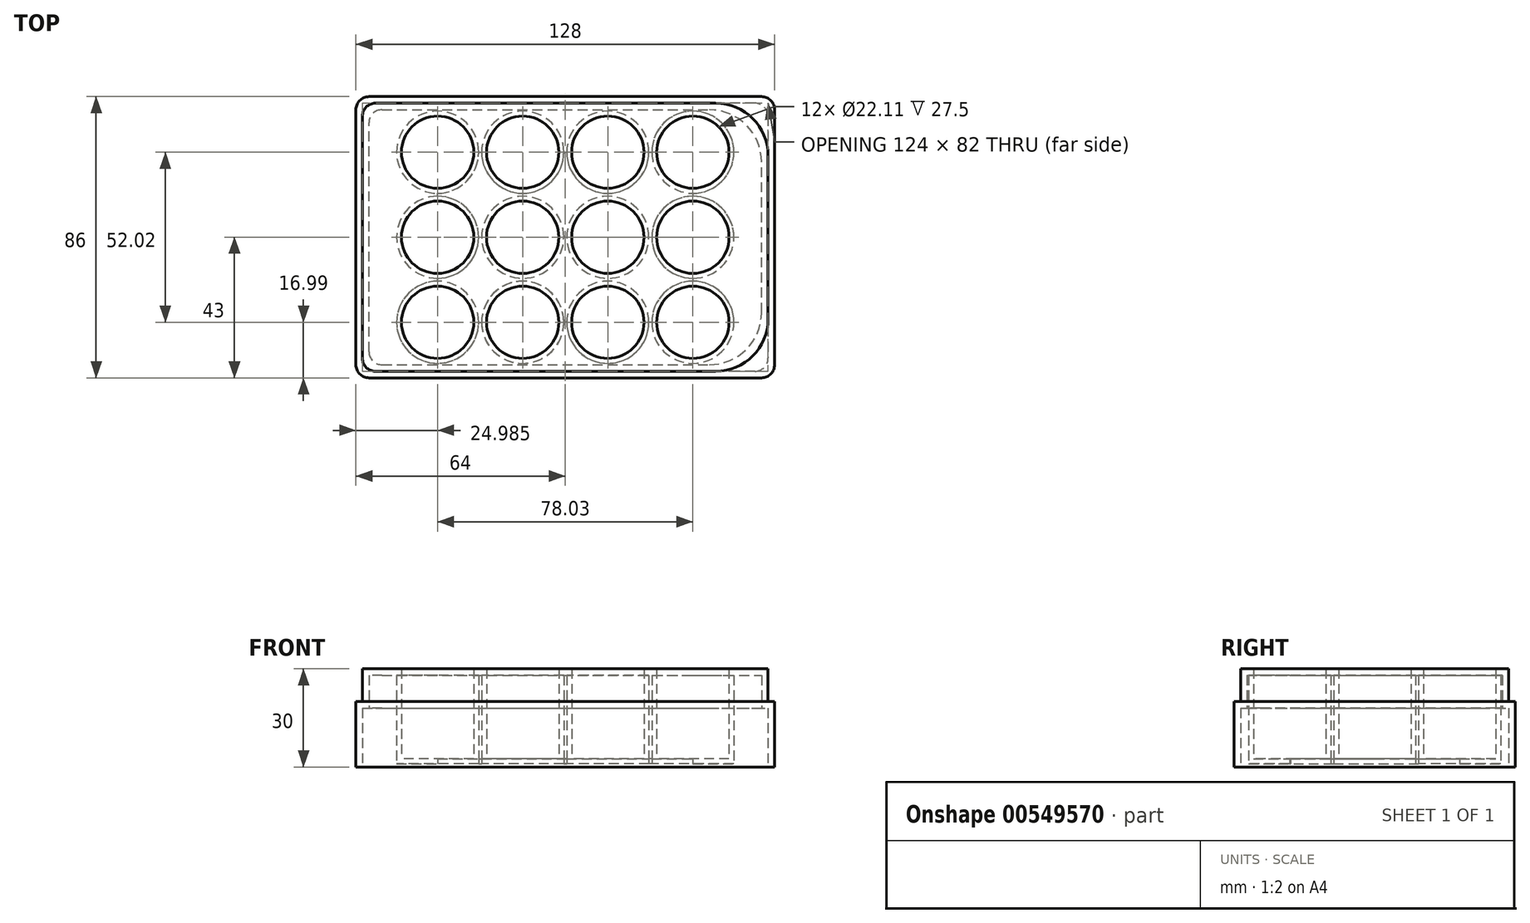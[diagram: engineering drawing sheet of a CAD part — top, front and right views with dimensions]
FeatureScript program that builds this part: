
annotation { "Feature Type Name" : "Feature", "Feature Type Description" : "" }
export const myFeature = defineFeature(function(context is Context, id is Id, definition is map)
    precondition{}
    {
        {
            var Q0;
            Q0=qCreatedBy(makeId("Top.planeOp"),FACE);
            var sketch = newSketch(context, id + "F0", { "sketchPlane" : qUnion([Q0])});
            skLineSegment(sketch, "E0.bottom", {"start": v(60, 43) * mm, "end": v(-60, 43) * mm});
            skLineSegment(sketch, "E0.top", {"start": v(64, -43) * mm, "end": v(-64, -43) * mm, "construction": true});
            skLineSegment(sketch, "E0.left", {"start": v(64, 39) * mm, "end": v(64, -39) * mm});
            skLineSegment(sketch, "E0.right", {"start": v(-64, 43) * mm, "end": v(-64, -39) * mm, "construction": true});
            skPoint(sketch, "E0.middle", {"position": v(0, 0) * mm});
            skLineSegment(sketch, "E1", {"start": v(-64, 26.01) * mm, "end": v(64, 26.01) * mm, "construction": true});
            skLineSegment(sketch, "E2", {"start": v(-64, 0) * mm, "end": v(64, 0) * mm, "construction": true});
            skLineSegment(sketch, "E3", {"start": v(-64, -26.01) * mm, "end": v(64, -26) * mm, "construction": true});
            skLineSegment(sketch, "E4", {"start": v(-39.02, -43) * mm, "end": v(-39.02, 43) * mm, "construction": true});
            skLineSegment(sketch, "E5", {"start": v(-13, -43) * mm, "end": v(-13, 43) * mm, "construction": true});
            skLineSegment(sketch, "E6", {"start": v(13, -43) * mm, "end": v(13, 43) * mm, "construction": true});
            skLineSegment(sketch, "E7", {"start": v(39.02, -43) * mm, "end": v(39.02, 43) * mm, "construction": true});
            skCircle(sketch, "E8", {"center": v(-39.02, 26.01) * mm, "radius": 11.05 * mm});
            skCircle(sketch, "E9", {"center": v(-13, 26.01) * mm, "radius": 11.05 * mm});
            skCircle(sketch, "E10", {"center": v(13, 26.01) * mm, "radius": 11.05 * mm});
            skCircle(sketch, "E11", {"center": v(39.02, 26.01) * mm, "radius": 11.05 * mm});
            skCircle(sketch, "E12", {"center": v(-13, 0) * mm, "radius": 11.05 * mm});
            skCircle(sketch, "E13", {"center": v(13, 0) * mm, "radius": 11.05 * mm});
            skCircle(sketch, "E14", {"center": v(39.02, 0) * mm, "radius": 11.05 * mm});
            skCircle(sketch, "E15", {"center": v(-13, -26) * mm, "radius": 11.05 * mm});
            skCircle(sketch, "E16", {"center": v(13, -26) * mm, "radius": 11.05 * mm});
            skCircle(sketch, "E17", {"center": v(39.02, -26) * mm, "radius": 11.05 * mm});
            skCircle(sketch, "E18", {"center": v(-39.02, 0) * mm, "radius": 11.05 * mm});
            skCircle(sketch, "E19", {"center": v(-39.02, -26) * mm, "radius": 11.05 * mm});
            skLineSegment(sketch, "E20", {"start": v(-64, 39) * mm, "end": v(-64, 26.01) * mm, "construction": true});
            skLineSegment(sketch, "E21", {"start": v(-64, 26.01) * mm, "end": v(-64, 0) * mm, "construction": true});
            skLineSegment(sketch, "E22", {"start": v(-64, 0) * mm, "end": v(-64, -26.01) * mm, "construction": true});
            skLineSegment(sketch, "E23", {"start": v(-60, -43) * mm, "end": v(-39.02, -43) * mm, "construction": true});
            skLineSegment(sketch, "E24", {"start": v(-39.02, -43) * mm, "end": v(-13, -43) * mm, "construction": true});
            skLineSegment(sketch, "E25", {"start": v(-13, -43) * mm, "end": v(13, -43) * mm, "construction": true});
            skLineSegment(sketch, "E26", {"start": v(13, -43) * mm, "end": v(39.02, -43) * mm, "construction": true});
            skLineSegment(sketch, "E27", {"start": v(39.02, -43) * mm, "end": v(60, -43) * mm, "construction": true});
            skPoint(sketch, "E28.visualSharp", {"position": v(-64, 43) * mm});
            skArc(sketch, "E28.filletArc", {"start": v(-60, 43) * mm, "mid": v(-62.83, 41.83) * mm, "end": v(-64, 39) * mm});
            skPoint(sketch, "E29.visualSharp", {"position": v(-64, -43) * mm});
            skArc(sketch, "E29.filletArc", {"start": v(-64, -39) * mm, "mid": v(-62.83, -41.83) * mm, "end": v(-60, -43) * mm});
            skPoint(sketch, "E30.visualSharp", {"position": v(64, -43) * mm});
            skArc(sketch, "E30.filletArc", {"start": v(60, -43) * mm, "mid": v(62.83, -41.83) * mm, "end": v(64, -39) * mm});
            skPoint(sketch, "E31.visualSharp", {"position": v(64, 43) * mm});
            skArc(sketch, "E31.filletArc", {"start": v(64, 39) * mm, "mid": v(62.83, 41.83) * mm, "end": v(60, 43) * mm});
            skLineSegment(sketch, "E32", {"start": v(-64, -39) * mm, "end": v(-64, -26.01) * mm, "construction": true});
            skLineSegment(sketch, "E33", {"start": v(-64, 39) * mm, "end": v(-64, -39) * mm});
            skLineSegment(sketch, "E34", {"start": v(-60, -43) * mm, "end": v(60, -43) * mm});
            skLineSegment(sketch, "E35.bottom", {"start": v(46, 41) * mm, "end": v(-58, 41) * mm});
            skLineSegment(sketch, "E35.top", {"start": v(46, -41) * mm, "end": v(-58, -41) * mm});
            skLineSegment(sketch, "E35.left", {"start": v(62, 25) * mm, "end": v(62, -25) * mm});
            skLineSegment(sketch, "E35.right", {"start": v(-62, 37) * mm, "end": v(-62, -37) * mm});
            skPoint(sketch, "E36.visualSharp", {"position": v(-62, 41) * mm});
            skArc(sketch, "E36.filletArc", {"start": v(-58, 41) * mm, "mid": v(-60.83, 39.83) * mm, "end": v(-62, 37) * mm});
            skPoint(sketch, "E37.visualSharp", {"position": v(-62, -41) * mm});
            skArc(sketch, "E37.filletArc", {"start": v(-62, -37) * mm, "mid": v(-60.83, -39.83) * mm, "end": v(-58, -41) * mm});
            skPoint(sketch, "E38.visualSharp", {"position": v(62, -41) * mm});
            skArc(sketch, "E38.filletArc", {"start": v(46, -41) * mm, "mid": v(57.31, -36.31) * mm, "end": v(62, -25) * mm});
            skPoint(sketch, "E39.visualSharp", {"position": v(62, 41) * mm});
            skArc(sketch, "E39.filletArc", {"start": v(62, 25) * mm, "mid": v(57.31, 36.31) * mm, "end": v(46, 41) * mm});
            skLineSegment(sketch, "E40", {"start": v(-58, 41) * mm, "end": v(58, 41) * mm});
            skLineSegment(sketch, "E41", {"start": v(62, 37) * mm, "end": v(62, -37) * mm});
            skLineSegment(sketch, "E42", {"start": v(58, -41) * mm, "end": v(-58, -41) * mm});
            skArc(sketch, "E43.filletArc", {"start": v(62, 37) * mm, "mid": v(60.83, 39.83) * mm, "end": v(58, 41) * mm});
            skArc(sketch, "E44.filletArc", {"start": v(58, -41) * mm, "mid": v(60.83, -39.83) * mm, "end": v(62, -37) * mm});
            skLineSegment(sketch, "E45.bottom", {"start": v(-56, -39) * mm, "end": v(44, -39) * mm});
            skLineSegment(sketch, "E45.top", {"start": v(-56, 39) * mm, "end": v(44, 39) * mm});
            skLineSegment(sketch, "E45.left", {"start": v(-60, -35) * mm, "end": v(-60, 35) * mm});
            skLineSegment(sketch, "E45.right", {"start": v(60, -23) * mm, "end": v(60, 23) * mm});
            skArc(sketch, "E46.filletArc", {"start": v(-60, -35) * mm, "mid": v(-58.83, -37.83) * mm, "end": v(-56, -39) * mm});
            skArc(sketch, "E47.filletArc", {"start": v(-56, 39) * mm, "mid": v(-58.83, 37.83) * mm, "end": v(-60, 35) * mm});
            skArc(sketch, "E48.filletArc", {"start": v(60, 23) * mm, "mid": v(55.31, 34.31) * mm, "end": v(44, 39) * mm});
            skArc(sketch, "E49.filletArc", {"start": v(44, -39) * mm, "mid": v(55.31, -34.31) * mm, "end": v(60, -23) * mm});
            skCircle(sketch, "E50", {"center": v(-39.02, -26) * mm, "radius": 12.55 * mm});
            skCircle(sketch, "E51", {"center": v(-13, 0) * mm, "radius": 12.55 * mm});
            skCircle(sketch, "E52", {"center": v(-13, 26) * mm, "radius": 12.55 * mm});
            skCircle(sketch, "E53", {"center": v(13, -26.01) * mm, "radius": 12.55 * mm});
            skCircle(sketch, "E54", {"center": v(13, 0) * mm, "radius": 12.55 * mm});
            skCircle(sketch, "E55", {"center": v(13, 26) * mm, "radius": 12.55 * mm});
            skCircle(sketch, "E56", {"center": v(39.02, -26.01) * mm, "radius": 12.55 * mm});
            skCircle(sketch, "E57", {"center": v(39.02, 26) * mm, "radius": 12.55 * mm});
            skCircle(sketch, "E58", {"center": v(39.02, 0) * mm, "radius": 12.55 * mm});
            skCircle(sketch, "E59", {"center": v(-13, -26.01) * mm, "radius": 12.55 * mm});
            skCircle(sketch, "E60", {"center": v(-39.02, 26) * mm, "radius": 12.55 * mm});
            skCircle(sketch, "E61", {"center": v(-39.02, 0) * mm, "radius": 12.55 * mm});
            skLineSegment(sketch, "E62", {"start": v(-39.02, -13.46) * mm, "end": v(-39.02, -12.56) * mm});
            skLineSegment(sketch, "E63", {"start": v(-26.46, -26) * mm, "end": v(-25.56, -26) * mm});
            skLineSegment(sketch, "E64", {"start": v(-39.02, 12.55) * mm, "end": v(-39.02, 13.45) * mm});
            skLineSegment(sketch, "E65", {"start": v(-26.46, 26.01) * mm, "end": v(-25.56, 26.01) * mm});
            skLineSegment(sketch, "E66", {"start": v(-0.45, 26.01) * mm, "end": v(0.45, 26.01) * mm});
            skLineSegment(sketch, "E67", {"start": v(25.56, 26.01) * mm, "end": v(26.46, 26.01) * mm});
            skLineSegment(sketch, "E68", {"start": v(39.02, 13.45) * mm, "end": v(39.02, 12.55) * mm});
            skLineSegment(sketch, "E69", {"start": v(39.02, -12.56) * mm, "end": v(39.02, -13.46) * mm});
            skLineSegment(sketch, "E70", {"start": v(26.46, -26) * mm, "end": v(25.56, -26) * mm});
            skLineSegment(sketch, "E71", {"start": v(0.45, -26.01) * mm, "end": v(-0.45, -25.7) * mm});
            skSolve(sketch);
        }
        {
            var Q0;
            Q0=makeQuery(id+"F0.imprint","IMPRINT",FACE,{"disambiguationData":[TD([[makeQuery(id+"F0.imprint","IMPRINT",EDGE,{"derivedFrom":sQuery(id+"F0.wireOp",EDGE,"E0.bottom")}),1.0]])]});
            extrude(context, id + "F1", {"entities" : qUnion([Q0]), "depth" : 20 * mm});
        }
        {
            var Q0;
            {var subQ0=sQuery(id+"F0.wireOp",EDGE,"E39.filletArc");Q0=makeQuery(id+"F0.imprint","IMPRINT",FACE,{"disambiguationData":[TD([[makeQuery(id+"F0.imprint","IMPRINT",EDGE,{"derivedFrom":subQ0}),-1.0]])]});}
            var Q1;
            {var subQ0=sQuery(id+"F0.wireOp",EDGE,"E38.filletArc");Q1=makeQuery(id+"F0.imprint","IMPRINT",FACE,{"disambiguationData":[TD([[makeQuery(id+"F0.imprint","IMPRINT",EDGE,{"derivedFrom":subQ0}),-1.0]])]});}
            extrude(context, id + "F2", {"entities" : qUnion([Q0, Q1]), "operationType" : NewBodyOperationType.ADD, "depth" : 20 * mm});
        }
        {
            var Q0;
            {var subQ0=sQuery(id+"F0.wireOp",EDGE,"E39.filletArc");Q0=makeQuery(id+"F0.imprint","IMPRINT",FACE,{"disambiguationData":[TD([[makeQuery(id+"F0.imprint","IMPRINT",EDGE,{"derivedFrom":subQ0}),-1.0]])]});}
            var Q1;
            {var subQ0=sQuery(id+"F0.wireOp",EDGE,"E38.filletArc");Q1=makeQuery(id+"F0.imprint","IMPRINT",FACE,{"disambiguationData":[TD([[makeQuery(id+"F0.imprint","IMPRINT",EDGE,{"derivedFrom":subQ0}),-1.0]])]});}
            extrude(context, id + "F3", {"entities" : qUnion([Q0, Q1]), "operationType" : NewBodyOperationType.REMOVE, "depth" : 18 * mm});
        }
        {
            var Q0;
            Q0=makeQuery(id+"F0.imprint","IMPRINT",FACE,{"disambiguationData":[TD([[makeQuery(id+"F0.imprint","IMPRINT",EDGE,{"derivedFrom":sQuery(id+"F0.wireOp",EDGE,"E35.right")}),1.0]])]});
            var Q1;
            Q1=makeQuery(id+"F0.imprint","IMPRINT",FACE,{"disambiguationData":[TD([[makeQuery(id+"F0.imprint","IMPRINT",EDGE,{"derivedFrom":sQuery(id+"F0.wireOp",EDGE,"E45.bottom")}),1.0]])]});
            var Q2;
            Q2=makeQuery(id+"F0.imprint","IMPRINT",FACE,{"disambiguationData":[TD([[makeQuery(id+"F0.imprint","IMPRINT",EDGE,{"derivedFrom":sQuery(id+"F0.wireOp",EDGE,"E51")}),-1.0]])]});
            extrude(context, id + "F4", {"entities" : qUnion([Q0, Q1, Q2]), "operationType" : NewBodyOperationType.ADD, "depth" : 30 * mm});
        }
        {
            var Q0;
            Q0=makeQuery(id+"F0.imprint","IMPRINT",FACE,{"disambiguationData":[TD([[makeQuery(id+"F0.imprint","IMPRINT",EDGE,{"derivedFrom":sQuery(id+"F0.wireOp",EDGE,"E35.right")}),1.0]])]});
            extrude(context, id + "F5", {"entities" : qUnion([Q0]), "operationType" : NewBodyOperationType.REMOVE, "depth" : 18 * mm});
        }
        {
            var Q0;
            Q0=makeQuery(id+"F0.imprint","IMPRINT",FACE,{"disambiguationData":[TD([[makeQuery(id+"F0.imprint","IMPRINT",EDGE,{"derivedFrom":sQuery(id+"F0.wireOp",EDGE,"E45.bottom")}),1.0]])]});
            var Q1;
            Q1=makeQuery(id+"F0.imprint","IMPRINT",FACE,{"disambiguationData":[TD([[makeQuery(id+"F0.imprint","IMPRINT",EDGE,{"derivedFrom":sQuery(id+"F0.wireOp",EDGE,"E51")}),-1.0]])]});
            extrude(context, id + "F6", {"entities" : qUnion([Q0, Q1]), "operationType" : NewBodyOperationType.REMOVE, "depth" : 28 * mm});
        }
        {
            var Q0;
            Q0=makeQuery(id+"F0.imprint","IMPRINT",FACE,{"disambiguationData":[TD([[makeQuery(id+"F0.imprint","IMPRINT",EDGE,{"derivedFrom":sQuery(id+"F0.wireOp",EDGE,"E19")}),-1.0]])]});
            var Q1;
            Q1=makeQuery(id+"F0.imprint","IMPRINT",FACE,{"disambiguationData":[TD([[makeQuery(id+"F0.imprint","IMPRINT",EDGE,{"derivedFrom":sQuery(id+"F0.wireOp",EDGE,"E15")}),-1.0]])]});
            var Q2;
            Q2=makeQuery(id+"F0.imprint","IMPRINT",FACE,{"disambiguationData":[TD([[makeQuery(id+"F0.imprint","IMPRINT",EDGE,{"derivedFrom":sQuery(id+"F0.wireOp",EDGE,"E18")}),-1.0]])]});
            var Q3;
            Q3=makeQuery(id+"F0.imprint","IMPRINT",FACE,{"disambiguationData":[TD([[makeQuery(id+"F0.imprint","IMPRINT",EDGE,{"derivedFrom":sQuery(id+"F0.wireOp",EDGE,"E12")}),-1.0]])]});
            var Q4;
            Q4=makeQuery(id+"F0.imprint","IMPRINT",FACE,{"disambiguationData":[TD([[makeQuery(id+"F0.imprint","IMPRINT",EDGE,{"derivedFrom":sQuery(id+"F0.wireOp",EDGE,"E13")}),-1.0]])]});
            var Q5;
            Q5=makeQuery(id+"F0.imprint","IMPRINT",FACE,{"disambiguationData":[TD([[makeQuery(id+"F0.imprint","IMPRINT",EDGE,{"derivedFrom":sQuery(id+"F0.wireOp",EDGE,"E16")}),-1.0]])]});
            var Q6;
            Q6=makeQuery(id+"F0.imprint","IMPRINT",FACE,{"disambiguationData":[TD([[makeQuery(id+"F0.imprint","IMPRINT",EDGE,{"derivedFrom":sQuery(id+"F0.wireOp",EDGE,"E17")}),-1.0]])]});
            var Q7;
            Q7=makeQuery(id+"F0.imprint","IMPRINT",FACE,{"disambiguationData":[TD([[makeQuery(id+"F0.imprint","IMPRINT",EDGE,{"derivedFrom":sQuery(id+"F0.wireOp",EDGE,"E14")}),-1.0]])]});
            var Q8;
            Q8=makeQuery(id+"F0.imprint","IMPRINT",FACE,{"disambiguationData":[TD([[makeQuery(id+"F0.imprint","IMPRINT",EDGE,{"derivedFrom":sQuery(id+"F0.wireOp",EDGE,"E11")}),-1.0]])]});
            var Q9;
            Q9=makeQuery(id+"F0.imprint","IMPRINT",FACE,{"disambiguationData":[TD([[makeQuery(id+"F0.imprint","IMPRINT",EDGE,{"derivedFrom":sQuery(id+"F0.wireOp",EDGE,"E10")}),-1.0]])]});
            var Q10;
            Q10=makeQuery(id+"F0.imprint","IMPRINT",FACE,{"disambiguationData":[TD([[makeQuery(id+"F0.imprint","IMPRINT",EDGE,{"derivedFrom":sQuery(id+"F0.wireOp",EDGE,"E9")}),-1.0]])]});
            var Q11;
            Q11=makeQuery(id+"F0.imprint","IMPRINT",FACE,{"disambiguationData":[TD([[makeQuery(id+"F0.imprint","IMPRINT",EDGE,{"derivedFrom":sQuery(id+"F0.wireOp",EDGE,"E8")}),-1.0]])]});
            extrude(context, id + "F7", {"entities" : qUnion([Q0, Q1, Q2, Q3, Q4, Q5, Q6, Q7, Q8, Q9, Q10, Q11]), "operationType" : NewBodyOperationType.ADD, "depth" : 30 * mm});
        }
        {
            var Q0;
            Q0=makeQuery(id+"F0.imprint","IMPRINT",FACE,{"disambiguationData":[TD([[makeQuery(id+"F0.imprint","IMPRINT",EDGE,{"derivedFrom":sQuery(id+"F0.wireOp",EDGE,"E19")}),1.0]])]});
            var Q1;
            Q1=makeQuery(id+"F0.imprint","IMPRINT",FACE,{"disambiguationData":[TD([[makeQuery(id+"F0.imprint","IMPRINT",EDGE,{"derivedFrom":sQuery(id+"F0.wireOp",EDGE,"E51")}),-1.0]])]});
            var Q2;
            Q2=makeQuery(id+"F0.imprint","IMPRINT",FACE,{"disambiguationData":[TD([[makeQuery(id+"F0.imprint","IMPRINT",EDGE,{"derivedFrom":sQuery(id+"F0.wireOp",EDGE,"E15")}),1.0]])]});
            var Q3;
            Q3=makeQuery(id+"F0.imprint","IMPRINT",FACE,{"disambiguationData":[TD([[makeQuery(id+"F0.imprint","IMPRINT",EDGE,{"derivedFrom":sQuery(id+"F0.wireOp",EDGE,"E16")}),1.0]])]});
            var Q4;
            Q4=makeQuery(id+"F0.imprint","IMPRINT",FACE,{"disambiguationData":[TD([[makeQuery(id+"F0.imprint","IMPRINT",EDGE,{"derivedFrom":sQuery(id+"F0.wireOp",EDGE,"E17")}),1.0]])]});
            var Q5;
            Q5=makeQuery(id+"F0.imprint","IMPRINT",FACE,{"disambiguationData":[TD([[makeQuery(id+"F0.imprint","IMPRINT",EDGE,{"derivedFrom":sQuery(id+"F0.wireOp",EDGE,"E14")}),1.0]])]});
            var Q6;
            Q6=makeQuery(id+"F0.imprint","IMPRINT",FACE,{"disambiguationData":[TD([[makeQuery(id+"F0.imprint","IMPRINT",EDGE,{"derivedFrom":sQuery(id+"F0.wireOp",EDGE,"E13")}),1.0]])]});
            var Q7;
            Q7=makeQuery(id+"F0.imprint","IMPRINT",FACE,{"disambiguationData":[TD([[makeQuery(id+"F0.imprint","IMPRINT",EDGE,{"derivedFrom":sQuery(id+"F0.wireOp",EDGE,"E12")}),1.0]])]});
            var Q8;
            Q8=makeQuery(id+"F0.imprint","IMPRINT",FACE,{"disambiguationData":[TD([[makeQuery(id+"F0.imprint","IMPRINT",EDGE,{"derivedFrom":sQuery(id+"F0.wireOp",EDGE,"E18")}),1.0]])]});
            var Q9;
            Q9=makeQuery(id+"F0.imprint","IMPRINT",FACE,{"disambiguationData":[TD([[makeQuery(id+"F0.imprint","IMPRINT",EDGE,{"derivedFrom":sQuery(id+"F0.wireOp",EDGE,"E8")}),1.0]])]});
            var Q10;
            Q10=makeQuery(id+"F0.imprint","IMPRINT",FACE,{"disambiguationData":[TD([[makeQuery(id+"F0.imprint","IMPRINT",EDGE,{"derivedFrom":sQuery(id+"F0.wireOp",EDGE,"E9")}),1.0]])]});
            var Q11;
            Q11=makeQuery(id+"F0.imprint","IMPRINT",FACE,{"disambiguationData":[TD([[makeQuery(id+"F0.imprint","IMPRINT",EDGE,{"derivedFrom":sQuery(id+"F0.wireOp",EDGE,"E10")}),1.0]])]});
            var Q12;
            Q12=makeQuery(id+"F0.imprint","IMPRINT",FACE,{"disambiguationData":[TD([[makeQuery(id+"F0.imprint","IMPRINT",EDGE,{"derivedFrom":sQuery(id+"F0.wireOp",EDGE,"E11")}),1.0]])]});
            extrude(context, id + "F8", {"entities" : qUnion([Q0, Q1, Q2, Q3, Q4, Q5, Q6, Q7, Q8, Q9, Q10, Q11, Q12]), "operationType" : NewBodyOperationType.ADD, "depth" : 2.5 * mm, "offsetDistance" : 25 * mm});
        }
        {
            var Q0;
            Q0=makeQuery(id+"F0.imprint","IMPRINT",FACE,{"disambiguationData":[TD([[makeQuery(id+"F0.imprint","IMPRINT",EDGE,{"derivedFrom":sQuery(id+"F0.wireOp",EDGE,"E19")}),-1.0]])]});
            var Q1;
            Q1=makeQuery(id+"F0.imprint","IMPRINT",FACE,{"disambiguationData":[TD([[makeQuery(id+"F0.imprint","IMPRINT",EDGE,{"derivedFrom":sQuery(id+"F0.wireOp",EDGE,"E15")}),-1.0]])]});
            var Q2;
            Q2=makeQuery(id+"F0.imprint","IMPRINT",FACE,{"disambiguationData":[TD([[makeQuery(id+"F0.imprint","IMPRINT",EDGE,{"derivedFrom":sQuery(id+"F0.wireOp",EDGE,"E51")}),-1.0]])]});
            var Q3;
            Q3=makeQuery(id+"F0.imprint","IMPRINT",FACE,{"disambiguationData":[TD([[makeQuery(id+"F0.imprint","IMPRINT",EDGE,{"derivedFrom":sQuery(id+"F0.wireOp",EDGE,"E19")}),1.0]])]});
            var Q4;
            Q4=makeQuery(id+"F0.imprint","IMPRINT",FACE,{"disambiguationData":[TD([[makeQuery(id+"F0.imprint","IMPRINT",EDGE,{"derivedFrom":sQuery(id+"F0.wireOp",EDGE,"E16")}),-1.0]])]});
            var Q5;
            Q5=makeQuery(id+"F0.imprint","IMPRINT",FACE,{"disambiguationData":[TD([[makeQuery(id+"F0.imprint","IMPRINT",EDGE,{"derivedFrom":sQuery(id+"F0.wireOp",EDGE,"E17")}),-1.0]])]});
            var Q6;
            Q6=makeQuery(id+"F0.imprint","IMPRINT",FACE,{"disambiguationData":[TD([[makeQuery(id+"F0.imprint","IMPRINT",EDGE,{"derivedFrom":sQuery(id+"F0.wireOp",EDGE,"E14")}),-1.0]])]});
            var Q7;
            Q7=makeQuery(id+"F0.imprint","IMPRINT",FACE,{"disambiguationData":[TD([[makeQuery(id+"F0.imprint","IMPRINT",EDGE,{"derivedFrom":sQuery(id+"F0.wireOp",EDGE,"E11")}),-1.0]])]});
            var Q8;
            Q8=makeQuery(id+"F0.imprint","IMPRINT",FACE,{"disambiguationData":[TD([[makeQuery(id+"F0.imprint","IMPRINT",EDGE,{"derivedFrom":sQuery(id+"F0.wireOp",EDGE,"E10")}),-1.0]])]});
            var Q9;
            Q9=makeQuery(id+"F0.imprint","IMPRINT",FACE,{"disambiguationData":[TD([[makeQuery(id+"F0.imprint","IMPRINT",EDGE,{"derivedFrom":sQuery(id+"F0.wireOp",EDGE,"E9")}),-1.0]])]});
            var Q10;
            Q10=makeQuery(id+"F0.imprint","IMPRINT",FACE,{"disambiguationData":[TD([[makeQuery(id+"F0.imprint","IMPRINT",EDGE,{"derivedFrom":sQuery(id+"F0.wireOp",EDGE,"E8")}),-1.0]])]});
            var Q11;
            Q11=makeQuery(id+"F0.imprint","IMPRINT",FACE,{"disambiguationData":[TD([[makeQuery(id+"F0.imprint","IMPRINT",EDGE,{"derivedFrom":sQuery(id+"F0.wireOp",EDGE,"E18")}),-1.0]])]});
            var Q12;
            Q12=makeQuery(id+"F0.imprint","IMPRINT",FACE,{"disambiguationData":[TD([[makeQuery(id+"F0.imprint","IMPRINT",EDGE,{"derivedFrom":sQuery(id+"F0.wireOp",EDGE,"E12")}),1.0]])]});
            var Q13;
            Q13=makeQuery(id+"F0.imprint","IMPRINT",FACE,{"disambiguationData":[TD([[makeQuery(id+"F0.imprint","IMPRINT",EDGE,{"derivedFrom":sQuery(id+"F0.wireOp",EDGE,"E13")}),1.0]])]});
            var Q14;
            Q14=makeQuery(id+"F0.imprint","IMPRINT",FACE,{"disambiguationData":[TD([[makeQuery(id+"F0.imprint","IMPRINT",EDGE,{"derivedFrom":sQuery(id+"F0.wireOp",EDGE,"E15")}),1.0]])]});
            var Q15;
            Q15=makeQuery(id+"F0.imprint","IMPRINT",FACE,{"disambiguationData":[TD([[makeQuery(id+"F0.imprint","IMPRINT",EDGE,{"derivedFrom":sQuery(id+"F0.wireOp",EDGE,"E16")}),1.0]])]});
            var Q16;
            Q16=makeQuery(id+"F0.imprint","IMPRINT",FACE,{"disambiguationData":[TD([[makeQuery(id+"F0.imprint","IMPRINT",EDGE,{"derivedFrom":sQuery(id+"F0.wireOp",EDGE,"E17")}),1.0]])]});
            var Q17;
            Q17=makeQuery(id+"F0.imprint","IMPRINT",FACE,{"disambiguationData":[TD([[makeQuery(id+"F0.imprint","IMPRINT",EDGE,{"derivedFrom":sQuery(id+"F0.wireOp",EDGE,"E14")}),1.0]])]});
            var Q18;
            Q18=makeQuery(id+"F0.imprint","IMPRINT",FACE,{"disambiguationData":[TD([[makeQuery(id+"F0.imprint","IMPRINT",EDGE,{"derivedFrom":sQuery(id+"F0.wireOp",EDGE,"E13")}),-1.0]])]});
            var Q19;
            Q19=makeQuery(id+"F0.imprint","IMPRINT",FACE,{"disambiguationData":[TD([[makeQuery(id+"F0.imprint","IMPRINT",EDGE,{"derivedFrom":sQuery(id+"F0.wireOp",EDGE,"E12")}),-1.0]])]});
            var Q20;
            Q20=makeQuery(id+"F0.imprint","IMPRINT",FACE,{"disambiguationData":[TD([[makeQuery(id+"F0.imprint","IMPRINT",EDGE,{"derivedFrom":sQuery(id+"F0.wireOp",EDGE,"E18")}),1.0]])]});
            var Q21;
            Q21=makeQuery(id+"F0.imprint","IMPRINT",FACE,{"disambiguationData":[TD([[makeQuery(id+"F0.imprint","IMPRINT",EDGE,{"derivedFrom":sQuery(id+"F0.wireOp",EDGE,"E8")}),1.0]])]});
            var Q22;
            Q22=makeQuery(id+"F0.imprint","IMPRINT",FACE,{"disambiguationData":[TD([[makeQuery(id+"F0.imprint","IMPRINT",EDGE,{"derivedFrom":sQuery(id+"F0.wireOp",EDGE,"E9")}),1.0]])]});
            var Q23;
            Q23=makeQuery(id+"F0.imprint","IMPRINT",FACE,{"disambiguationData":[TD([[makeQuery(id+"F0.imprint","IMPRINT",EDGE,{"derivedFrom":sQuery(id+"F0.wireOp",EDGE,"E10")}),1.0]])]});
            var Q24;
            Q24=makeQuery(id+"F0.imprint","IMPRINT",FACE,{"disambiguationData":[TD([[makeQuery(id+"F0.imprint","IMPRINT",EDGE,{"derivedFrom":sQuery(id+"F0.wireOp",EDGE,"E11")}),1.0]])]});
            extrude(context, id + "F9", {"entities" : qUnion([Q0, Q1, Q2, Q3, Q4, Q5, Q6, Q7, Q8, Q9, Q10, Q11, Q12, Q13, Q14, Q15, Q16, Q17, Q18, Q19, Q20, Q21, Q22, Q23, Q24]), "operationType" : NewBodyOperationType.REMOVE, "depth" : 1 * mm, "offsetDistance" : 25 * mm});
        }
    });
